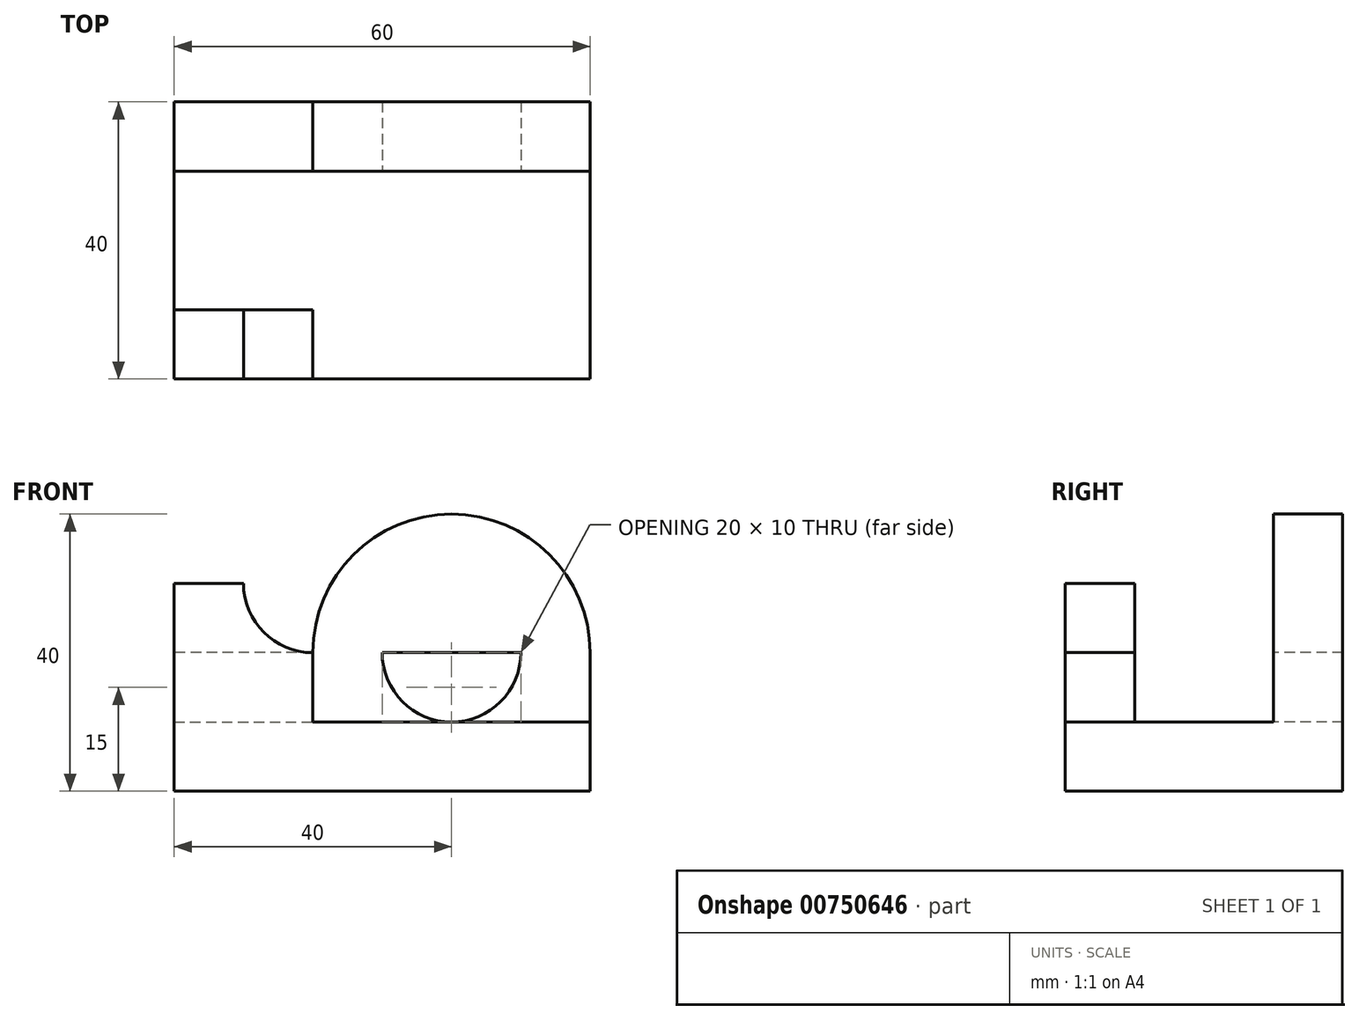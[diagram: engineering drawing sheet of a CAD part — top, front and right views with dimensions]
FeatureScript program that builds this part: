
annotation { "Feature Type Name" : "Feature", "Feature Type Description" : "" }
export const myFeature = defineFeature(function(context is Context, id is Id, definition is map)
    precondition{}
    {
        {
            var Q0;
            Q0=qCreatedBy(makeId("Top.planeOp"),FACE);
            var sketch = newSketch(context, id + "F0", { "sketchPlane" : qUnion([Q0])});
            skLineSegment(sketch, "E0", {"start": v(0, 0) * mm, "end": v(60, 0) * mm});
            skLineSegment(sketch, "E1", {"start": v(60, 0) * mm, "end": v(60, 40) * mm});
            skLineSegment(sketch, "E2", {"start": v(60, 40) * mm, "end": v(0, 40) * mm});
            skLineSegment(sketch, "E3", {"start": v(0, 40) * mm, "end": v(0, 0) * mm});
            skSolve(sketch);
        }
        {
            var Q0;
            Q0=makeQuery(id+"F0.imprint","IMPRINT",FACE,{"disambiguationData":[TD([[makeQuery(id+"F0.imprint","IMPRINT",EDGE,{"derivedFrom":sQuery(id+"F0.wireOp",EDGE,"E0")}),1.0]])]});
            extrude(context, id + "F1", {"entities" : qUnion([Q0]), "depth" : 30 * mm, "offsetDistance" : 25 * mm});
        }
        {
            var Q0;
            Q0=makeQuery(id+"F1.opExtrude","CAP_FACE",FACE,{"disambiguationData":[OSD([sQuery(id+"F0.wireOp",EDGE,"E0"),sQuery(id+"F0.wireOp",EDGE,"E1"),sQuery(id+"F0.wireOp",EDGE,"E2"),sQuery(id+"F0.wireOp",EDGE,"E3")])],"isStart":false});
            var sketch = newSketch(context, id + "F2", { "sketchPlane" : qUnion([Q0])});
            skLineSegment(sketch, "E4", {"start": v(0, 0) * mm, "end": v(20, 0) * mm});
            skLineSegment(sketch, "E5", {"start": v(20, 0) * mm, "end": v(20, 10) * mm});
            skLineSegment(sketch, "E6", {"start": v(20, 10) * mm, "end": v(0, 10) * mm});
            skLineSegment(sketch, "E7", {"start": v(0, 10) * mm, "end": v(0, 0) * mm});
            skLineSegment(sketch, "E8", {"start": v(0, 40) * mm, "end": v(0, 30) * mm});
            skLineSegment(sketch, "E9", {"start": v(0, 30) * mm, "end": v(60, 30) * mm});
            skLineSegment(sketch, "E10", {"start": v(60, 30) * mm, "end": v(60, 40) * mm});
            skLineSegment(sketch, "E11", {"start": v(60, 40) * mm, "end": v(0, 40) * mm});
            skSolve(sketch);
        }
        {
            var Q0;
            {var subQ3=sQuery(id+"F2.wireOp",EDGE,"E5");Q0=makeQuery(id+"F2.imprint","IMPRINT",FACE,{"disambiguationData":[TD([[makeQuery(id+"F2.imprint","IMPRINT",EDGE,{"derivedFrom":subQ3}),-1.0]])]});}
            extrude(context, id + "F3", {"entities" : qUnion([Q0]), "operationType" : NewBodyOperationType.REMOVE, "oppositeDirection" : true, "depth" : 20 * mm, "offsetDistance" : 25 * mm});
        }
        {
            var Q0;
            {var subQ0=sQuery(id+"F0.wireOp",EDGE,"E1");var subQ1=sQuery(id+"F0.wireOp",EDGE,"E2");var subQ2=sQuery(id+"F0.wireOp",EDGE,"E3");Q0=makeQuery(id+"F3.boolean.opBoolean","SPLIT",FACE,{"disambiguationData":[TD([makeQuery(id+"F1.opExtrude","SWEPT_FACE",FACE,{"disambiguationData":[OSD([subQ0])]})])],"derivedFrom":makeQuery(id+"F1.opExtrude","CAP_FACE",FACE,{"disambiguationData":[OSD([sQuery(id+"F0.wireOp",EDGE,"E0"),subQ0,subQ1,subQ2])],"isStart":false})});}
            var sketch = newSketch(context, id + "F4", { "sketchPlane" : qUnion([Q0])});
            skLineSegment(sketch, "E12", {"start": v(0, 40) * mm, "end": v(20, 40) * mm});
            skLineSegment(sketch, "E13", {"start": v(20, 40) * mm, "end": v(20, 30) * mm});
            skLineSegment(sketch, "E14", {"start": v(20, 30) * mm, "end": v(0, 30) * mm});
            skLineSegment(sketch, "E15", {"start": v(0, 30) * mm, "end": v(0, 40) * mm});
            skSolve(sketch);
        }
        {
            var Q0;
            Q0 = qSketchRegion(id + "F4", true);
            extrude(context, id + "F5", {"entities" : qUnion([Q0]), "operationType" : NewBodyOperationType.REMOVE, "oppositeDirection" : true, "depth" : 10 * mm, "offsetDistance" : 25 * mm});
        }
        {
            var Q0;
            Q0=makeQuery(id+"F3.boolean.opBoolean","COPY",FACE,{"derivedFrom":makeQuery(id+"F3.opExtrude","SWEPT_FACE",FACE,{"disambiguationData":[OSD([sQuery(id+"F2.wireOp",EDGE,"E9")])]})});
            var sketch = newSketch(context, id + "F6", { "sketchPlane" : qUnion([Q0])});
            skLineSegment(sketch, "E16", {"start": v(20, 20) * mm, "end": v(60, 20) * mm});
            skLineSegment(sketch, "E17", {"start": v(60, 20) * mm, "end": v(60, 30) * mm});
            skLineSegment(sketch, "E18", {"start": v(60, 30) * mm, "end": v(20, 30) * mm});
            skLineSegment(sketch, "E19", {"start": v(20, 30) * mm, "end": v(20, 20) * mm});
            skSolve(sketch);
        }
        {
            var Q0;
            Q0=makeQuery(id+"F6.imprint","IMPRINT",FACE,{"disambiguationData":[TD([[makeQuery(id+"F6.imprint","IMPRINT",EDGE,{"derivedFrom":sQuery(id+"F6.wireOp",EDGE,"E16")}),1.0]])]});
            extrude(context, id + "F7", {"entities" : qUnion([Q0]), "operationType" : NewBodyOperationType.REMOVE, "oppositeDirection" : true, "depth" : 25 * mm, "offsetDistance" : 25 * mm});
        }
        {
            var Q0;
            Q0=makeQuery(id+"F3.boolean.opBoolean","COPY",FACE,{"derivedFrom":makeQuery(id+"F3.opExtrude","SWEPT_FACE",FACE,{"disambiguationData":[OSD([sQuery(id+"F2.wireOp",EDGE,"E9")])]})});
            var sketch = newSketch(context, id + "F8", { "sketchPlane" : qUnion([Q0])});
            skArc(sketch, "E20", {"start": v(60, 20) * mm, "mid": v(40.02, 40.86) * mm, "end": v(20.04, 20) * mm});
            skSolve(sketch);
        }
        {
            var Q0;
            {var subQ0=sQuery(id+"F8.wireOp",EDGE,"E20");Q0=makeQuery(id+"F8.imprint","IMPRINT",FACE,{"disambiguationData":[TD([[makeQuery(id+"F8.imprint","IMPRINT",EDGE,{"derivedFrom":subQ0}),1.0]])]});}
            extrude(context, id + "F9", {"entities" : qUnion([Q0]), "oppositeDirection" : true, "depth" : 10 * mm, "offsetDistance" : 25 * mm});
        }
        {
            var Q0;
            Q0=makeQuery(id+"F1.opExtrude","SWEPT_FACE",FACE,{"disambiguationData":[OSD([sQuery(id+"F0.wireOp",EDGE,"E0")])]});
            var sketch = newSketch(context, id + "F10", { "sketchPlane" : qUnion([Q0])});
            skArc(sketch, "E21", {"start": v(10, 30) * mm, "mid": v(12.93, 22.93) * mm, "end": v(20, 20) * mm});
            skSolve(sketch);
        }
        {
            var Q0;
            {var subQ0=sQuery(id+"F10.wireOp",EDGE,"E21");Q0=makeQuery(id+"F10.imprint","IMPRINT",FACE,{"disambiguationData":[TD([[makeQuery(id+"F10.imprint","IMPRINT",EDGE,{"derivedFrom":subQ0}),1.0]])]});}
            extrude(context, id + "F11", {"entities" : qUnion([Q0]), "operationType" : NewBodyOperationType.REMOVE, "oppositeDirection" : true, "depth" : 11 * mm, "offsetDistance" : 25 * mm});
        }
        {
            var Q0;
            Q0=makeQuery(id+"F3.boolean.opBoolean","COPY",FACE,{"derivedFrom":makeQuery(id+"F3.opExtrude","SWEPT_FACE",FACE,{"disambiguationData":[OSD([sQuery(id+"F2.wireOp",EDGE,"E9")])]})});
            var sketch = newSketch(context, id + "F12", { "sketchPlane" : qUnion([Q0])});
            skLineSegment(sketch, "E22", {"start": v(60, 10) * mm, "end": v(40, 10) * mm});
            skLineSegment(sketch, "E23", {"start": v(40, 10) * mm, "end": v(20, 10) * mm});
            skLineSegment(sketch, "E24", {"start": v(20, 10) * mm, "end": v(20, 20) * mm});
            skLineSegment(sketch, "E25", {"start": v(20, 20) * mm, "end": v(40, 20) * mm});
            skLineSegment(sketch, "E26", {"start": v(40, 20) * mm, "end": v(60, 20) * mm});
            skLineSegment(sketch, "E27", {"start": v(60, 20) * mm, "end": v(60, 10) * mm});
            skCircle(sketch, "E28", {"center": v(40, 20) * mm, "radius": 10 * mm});
            skSolve(sketch);
        }
        {
            var Q0;
            {var subQ0=sQuery(id+"F12.wireOp",EDGE,"E26");var subQ1=sQuery(id+"F12.wireOp",EDGE,"E25");var subQ2=makeQuery(id+"F12.imprint","INTERSECT",VERTEX,{"derivedFrom":[subQ1,subQ0]});Q0=makeQuery(id+"F12.imprint","IMPRINT",FACE,{"disambiguationData":[TD([[makeQuery(id+"F12.imprint","IMPRINT",EDGE,{"disambiguationData":[TD([[subQ2,1.0]])],"derivedFrom":subQ1}),-1.0]])]});}
            var Q1;
            {var subQ0=sQuery(id+"F12.wireOp",EDGE,"E26");var subQ1=sQuery(id+"F12.wireOp",EDGE,"E25");var subQ2=makeQuery(id+"F12.imprint","INTERSECT",VERTEX,{"derivedFrom":[subQ1,subQ0]});Q1=makeQuery(id+"F12.imprint","IMPRINT",FACE,{"disambiguationData":[TD([[makeQuery(id+"F12.imprint","IMPRINT",EDGE,{"disambiguationData":[TD([[subQ2,1.0]])],"derivedFrom":subQ1}),1.0]])]});}
            extrude(context, id + "F13", {"entities" : qUnion([Q0, Q1]), "operationType" : NewBodyOperationType.REMOVE, "oppositeDirection" : true, "depth" : 15 * mm, "offsetDistance" : 25 * mm});
        }
        {
            var Q0;
            Q0=makeQuery(id+"F9.opExtrude","SWEPT_BODY",BODY,{"disambiguationData":[OSD([sQuery(id+"F4.wireOp",EDGE,"E14"),sQuery(id+"F6.wireOp",EDGE,"E16"),sQuery(id+"F8.wireOp",EDGE,"E20")])]});
            deleteBodies(context, id + "F14", {"entities" : qUnion([Q0])});
        }
        {
            var Q0;
            Q0=makeQuery(id+"F3.boolean.opBoolean","COPY",FACE,{"derivedFrom":makeQuery(id+"F3.opExtrude","SWEPT_FACE",FACE,{"disambiguationData":[OSD([sQuery(id+"F2.wireOp",EDGE,"E9")])]})});
            var sketch = newSketch(context, id + "F15", { "sketchPlane" : qUnion([Q0])});
            skLineSegment(sketch, "E29", {"start": v(60, 20) * mm, "end": v(60, 10) * mm});
            skLineSegment(sketch, "E30", {"start": v(60, 10) * mm, "end": v(20, 10) * mm});
            skLineSegment(sketch, "E31", {"start": v(20, 10) * mm, "end": v(20, 20) * mm});
            skLineSegment(sketch, "E32", {"start": v(20, 20) * mm, "end": v(60, 20) * mm});
            skArc(sketch, "E33", {"start": v(60, 20) * mm, "mid": v(40, 40) * mm, "end": v(20, 20) * mm});
            skSolve(sketch);
        }
        {
            var Q0;
            Q0=makeQuery(id+"F15.imprint","IMPRINT",FACE,{"disambiguationData":[TD([[makeQuery(id+"F15.imprint","IMPRINT",EDGE,{"derivedFrom":sQuery(id+"F15.wireOp",EDGE,"E32")}),1.0]])]});
            extrude(context, id + "F16", {"entities" : qUnion([Q0]), "operationType" : NewBodyOperationType.ADD, "oppositeDirection" : true, "depth" : 10 * mm, "offsetDistance" : 25 * mm});
        }
        {
            var Q0;
            Q0=makeQuery(id+"F16.boolean.opBoolean","MERGE",FACE,{"derivedFrom":[makeQuery(id+"F3.boolean.opBoolean","COPY",FACE,{"derivedFrom":makeQuery(id+"F3.opExtrude","SWEPT_FACE",FACE,{"disambiguationData":[OSD([sQuery(id+"F2.wireOp",EDGE,"E9")])]})}),makeQuery(id+"F16.opExtrude","CAP_FACE",FACE,{"disambiguationData":[OSD([sQuery(id+"F15.wireOp",EDGE,"E32"),sQuery(id+"F15.wireOp",EDGE,"E33")])],"isStart":true})]});
            var sketch = newSketch(context, id + "F17", { "sketchPlane" : qUnion([Q0])});
            skCircle(sketch, "E34", {"center": v(40, 20) * mm, "radius": 10 * mm});
            skSolve(sketch);
        }
        {
            var Q0;
            Q0=makeQuery(id+"F17.imprint","IMPRINT",FACE,{"disambiguationData":[TD([[makeQuery(id+"F17.imprint","IMPRINT",EDGE,{"derivedFrom":sQuery(id+"F17.wireOp",EDGE,"E34")}),1.0]])]});
            extrude(context, id + "F18", {"entities" : qUnion([Q0]), "operationType" : NewBodyOperationType.REMOVE, "oppositeDirection" : true, "depth" : 25 * mm, "offsetDistance" : 25 * mm});
        }
    });
